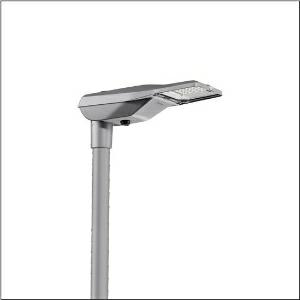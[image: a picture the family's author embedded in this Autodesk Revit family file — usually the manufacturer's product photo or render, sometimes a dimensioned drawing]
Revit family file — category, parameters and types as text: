
# Revit family: streetlight_sl_21_iq_micro___st1_0a_5xe1d31u08cb_b584
name_source: partatom
category: Lighting Fixtures
units: mm (PartAtom-declared; Revit-internal decimal feet)

## family parameters
Cut with Voids When Loaded = No
Host = Face
Light Source = No
Part Type = Normal
Room Calculation Point = No
Round Connector Dimension = Use Diameter
Shared = No

## types (1)
- --- (1 x LED, 2880 lm, 19.1 W, 3000K)
    Apparent Load = 19 VA
    CIE Flux Codes = 37 72 97 100 100
    Color Rendering = 70
    Color Temperature = 3000K
    Default Elevation = 1800 mm
    Description = Streetlight SL 21 iQ micro, mast luminaire, primary light control with lens, of PMMA, primary optical cover: cover, of toughened safety glass, transparent, light distribution: ST1.0a, light emission: direct distribution, primary light characteristic: asymmetric, installation type: post-top, side-entry, LED, High Power LED, rated luminous flux: 2.880lm, luminous efficacy: 151lm/W, light colour: 730, colour temperature: 3000K, control gear: iQ-Street Remote, D4i with power reduction, control: pre-setting: logarithmic dimming characteristic, Street-Remote, Auto-Match, Temp-Guard, Lumen-Switch, Night-Set, Smart-Wire, Light-Fading, Desk-Remote (wireless, voltage-free reading and setting of iQ features in the workshop via application-optimized NFC function/RFID function), optimised constant luminous flux control (CLO 2.0), mains connection: 220..240V, AC, 50/60Hz, start of lifetime: 19W, end of service life: 20W, reduction: 9W, luminaire housing, of diecast aluminium, powder-coated, SITECO metallic grey (DB 702S), corrosivity category C5 high according to DIN EN ISO 12944, please order mast flange separately, inclination adjustable: 0°, 5°, 10°, 15°, sealing non-destructively replaceable, multi-level sealing system, length: 528mm, width: 235mm, height: 110mm, mast flange for spigot size: 42mm (side-entry): 5XC10008XM4, 60/48mm (side-entry/post-top): 5XC10108XM2, 76/60mm (side-entry/post-top): 5XC10108XM1, mounting height: 4..8m, Smart Interface below, protection rating (complete): IP66, insulation class (complete): insulation class II (safety insulation), certification: CE, ENEC, ENEC+, VDE, impact resistance: IK10, permissible operating ambient temperature for outdoor applications: -40..+50°C, standard-compliant lighting for roads and squares, packaging unit: 1 piece

Light Distribution: ST1.0a
    Height = 110 mm
    Lamp = 1 x LED
    Lamp Light Flux = 2880 lm
    Lamp Power = 19.1 W
    Lamp count = 1
    Length = 528 mm
    Luminous efficacy = 151 lm/W
    Manufacturer = Siteco
    ModVariant = No
    Model = 5XE1D31U08CB
    Number of Poles = 1
    OnlyDefault = Yes
    Power Factor = 1
    Product Name = Streetlight SL 21 iQ micro | ST1.0a
    Product group = mast luminaire | pylon top
    ProductGroupID = 6100
    Protection Class = Protection class II
    Protection Degree = IP 66
    RLX_Detail_Level = 1
    RLX_Emergency_Light_Flux = 0 lm
    RLX_Emergency_Type = 0
    RLX_Emergency_Type_DB = No
    RlxData = <blob elided: 99413 chars, md5=625a9789>
    Socket = socket
    Standby Power = 0 W
    System Light Flux = 2880 lm
    System Power = 19 W
    Type Comments = factory setting: luminous flux: 100 % | dim-lin: 254 | 387 mA
    Type Image = l_1277290.jpg
    URL = http://relux.com
    VarID = @adj_115883
    Voltage = 0 V
    Weight = 0.00 kg
    Width = 235 mm

## geometry (parser evidence)
native form markers: Blend x4, Sweep x10
no freeform markers — native parametric forms only
